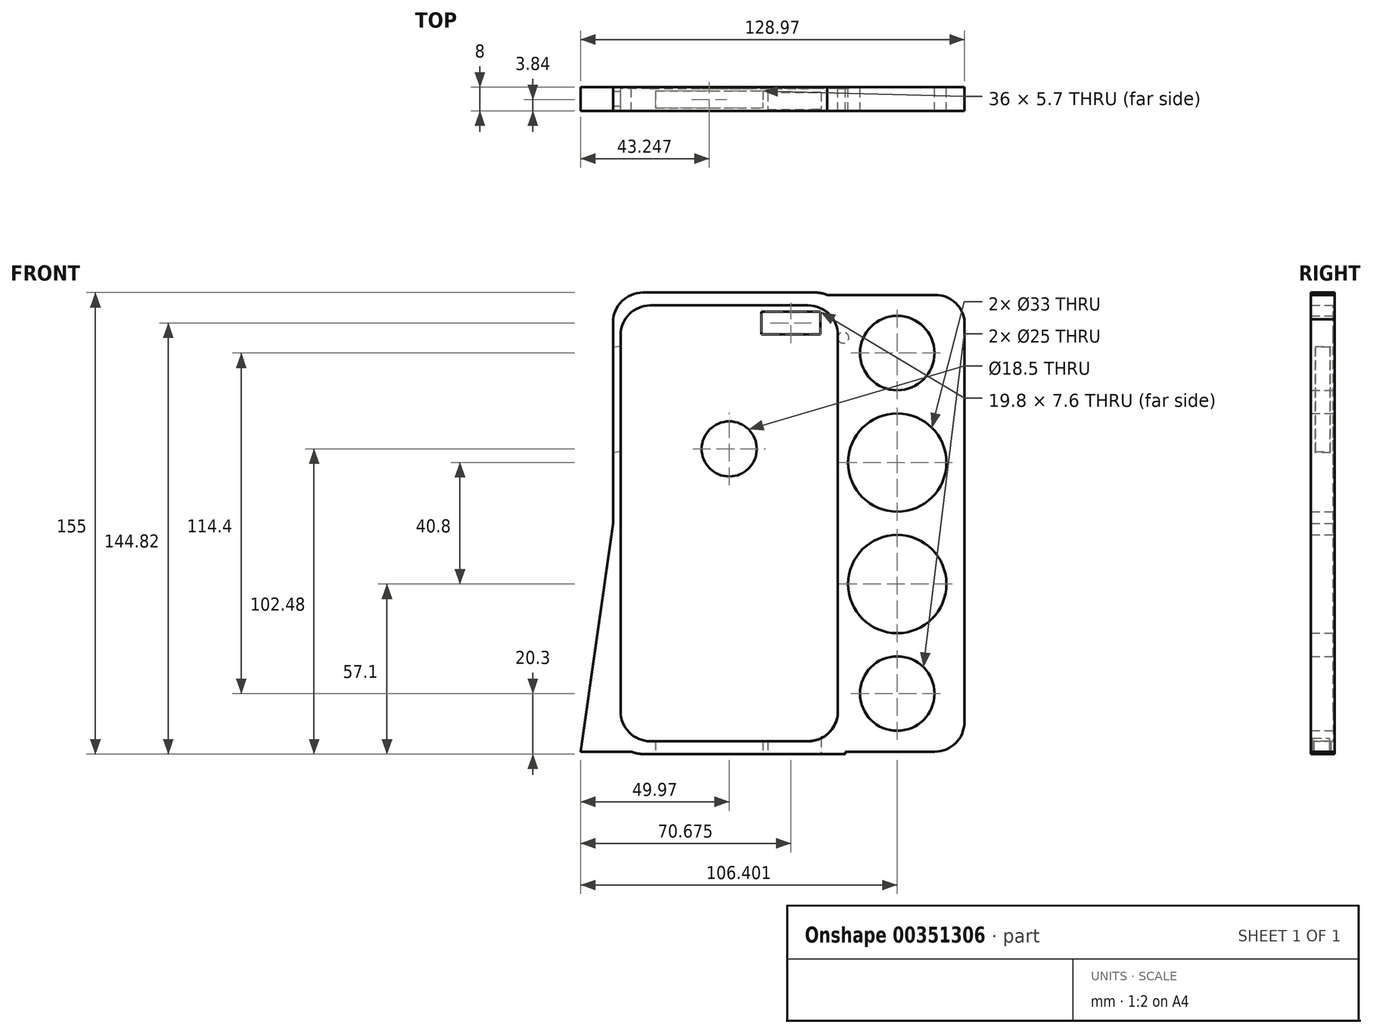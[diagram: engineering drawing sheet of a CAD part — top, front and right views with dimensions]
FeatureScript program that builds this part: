
annotation { "Feature Type Name" : "Feature", "Feature Type Description" : "" }
export const myFeature = defineFeature(function(context is Context, id is Id, definition is map)
    precondition{}
    {
        {
            var Q0;
            Q0=qCreatedBy(makeId("Front.planeOp"),FACE);
            var sketch = newSketch(context, id + "F0", { "sketchPlane" : qUnion([Q0])});
            skLineSegment(sketch, "E0.bottom", {"start": v(-29, -77.5) * mm, "end": v(39, -77.5) * mm});
            skLineSegment(sketch, "E0.top", {"start": v(-29, 77.5) * mm, "end": v(29, 77.5) * mm});
            skLineSegment(sketch, "E0.left", {"start": v(-39, -67.5) * mm, "end": v(-39, 67.5) * mm});
            skLineSegment(sketch, "E0.right", {"start": v(39, -77.5) * mm, "end": v(39, 77.5) * mm});
            skPoint(sketch, "E0.middle", {"position": v(0, 0) * mm});
            skLineSegment(sketch, "E1.bottom", {"start": v(39, 77.5) * mm, "end": v(79, 77.5) * mm});
            skLineSegment(sketch, "E1.top", {"start": v(39, -77.5) * mm, "end": v(79, -77.5) * mm});
            skLineSegment(sketch, "E1.left", {"start": v(39, 67.5) * mm, "end": v(39, -77.5) * mm});
            skLineSegment(sketch, "E1.right", {"start": v(79, 77.5) * mm, "end": v(79, -66.72) * mm});
            skCircle(sketch, "E2", {"center": v(56.43, 57.2) * mm, "radius": 12.5 * mm});
            skCircle(sketch, "E3", {"center": v(56.43, 20.4) * mm, "radius": 16.5 * mm});
            skCircle(sketch, "E4", {"center": v(56.43, -20.4) * mm, "radius": 16.5 * mm});
            skCircle(sketch, "E5", {"center": v(56.43, -57.2) * mm, "radius": 12.5 * mm});
            skPoint(sketch, "E6.visualSharp", {"position": v(-39, 77.5) * mm});
            skArc(sketch, "E6.filletArc", {"start": v(-29, 77.5) * mm, "mid": v(-36.07, 74.57) * mm, "end": v(-39, 67.5) * mm});
            skPoint(sketch, "E7.visualSharp", {"position": v(-39, -77.5) * mm});
            skArc(sketch, "E7.filletArc", {"start": v(-39, -67.5) * mm, "mid": v(-36.07, -74.57) * mm, "end": v(-29, -77.5) * mm});
            skPoint(sketch, "E8.visualSharp", {"position": v(39, 77.5) * mm});
            skArc(sketch, "E8.filletArc", {"start": v(39, 67.5) * mm, "mid": v(36.07, 74.57) * mm, "end": v(29, 77.5) * mm});
            skLineSegment(sketch, "E9.bottom", {"start": v(-49.97, -76.72) * mm, "end": v(69, -76.72) * mm});
            skLineSegment(sketch, "E9.top", {"start": v(-49.97, 76.72) * mm, "end": v(69.18, 76.72) * mm});
            skLineSegment(sketch, "E9.right", {"start": v(79.18, -76.72) * mm, "end": v(79.18, 66.72) * mm});
            skLineSegment(sketch, "E10", {"start": v(-49.97, 76.72) * mm, "end": v(-39, 0) * mm});
            skLineSegment(sketch, "E11", {"start": v(-39, 0) * mm, "end": v(-49.97, -76.72) * mm});
            skLineSegment(sketch, "E12.bottom", {"start": v(-26.5, -73.2) * mm, "end": v(26.5, -73.2) * mm});
            skLineSegment(sketch, "E12.top", {"start": v(-26.5, 73.2) * mm, "end": v(26.5, 73.2) * mm});
            skLineSegment(sketch, "E12.left", {"start": v(-36.5, -63.2) * mm, "end": v(-36.5, 63.2) * mm});
            skLineSegment(sketch, "E12.right", {"start": v(36.5, -63.2) * mm, "end": v(36.5, 63.2) * mm});
            skPoint(sketch, "E13.visualSharp", {"position": v(-36.5, 73.2) * mm});
            skArc(sketch, "E13.filletArc", {"start": v(-26.5, 73.2) * mm, "mid": v(-33.57, 70.26) * mm, "end": v(-36.5, 63.2) * mm});
            skPoint(sketch, "E14.visualSharp", {"position": v(36.5, 73.2) * mm});
            skArc(sketch, "E14.filletArc", {"start": v(36.5, 63.2) * mm, "mid": v(33.57, 70.26) * mm, "end": v(26.5, 73.2) * mm});
            skPoint(sketch, "E15.visualSharp", {"position": v(36.5, -73.2) * mm});
            skArc(sketch, "E15.filletArc", {"start": v(26.5, -73.2) * mm, "mid": v(33.57, -70.26) * mm, "end": v(36.5, -63.2) * mm});
            skPoint(sketch, "E16.visualSharp", {"position": v(-36.5, -73.2) * mm});
            skArc(sketch, "E16.filletArc", {"start": v(-36.5, -63.2) * mm, "mid": v(-33.57, -70.26) * mm, "end": v(-26.5, -73.2) * mm});
            skPoint(sketch, "E17.visualSharp", {"position": v(79.18, 76.72) * mm});
            skArc(sketch, "E17.filletArc", {"start": v(79.18, 66.72) * mm, "mid": v(76.25, 73.8) * mm, "end": v(69.18, 76.72) * mm});
            skPoint(sketch, "E18.newPointA", {"position": v(79.18, -76.72) * mm});
            skArc(sketch, "E18.filletArc", {"start": v(69, -76.72) * mm, "mid": v(76.07, -73.8) * mm, "end": v(79, -66.72) * mm});
            skPoint(sketch, "E9.left.end.orphan", {"position": v(-79.18, 76.72) * mm});
            skPoint(sketch, "E19.orphan", {"position": v(-79.18, -76.72) * mm});
            skSolve(sketch);
        }
        {
            var Q0;
            Q0=makeQuery(id+"F0.imprint","IMPRINT",FACE,{"disambiguationData":[TD([[makeQuery(id+"F0.imprint","IMPRINT",EDGE,{"derivedFrom":sQuery(id+"F0.wireOp",EDGE,"E12.bottom")}),1.0]])]});
            extrude(context, id + "F1", {"entities" : qUnion([Q0]), "depth" : .5 * mm});
        }
        {
            var Q0;
            {var subQ0=sQuery(id+"F0.wireOp",EDGE,"E0.bottom");Q0=makeQuery(id+"F0.imprint","IMPRINT",FACE,{"disambiguationData":[TD([[makeQuery(id+"F0.imprint","IMPRINT",EDGE,{"derivedFrom":subQ0}),1.0]])]});}
            var Q1;
            {var subQ0=sQuery(id+"F0.wireOp",EDGE,"E0.top");Q1=makeQuery(id+"F0.imprint","IMPRINT",FACE,{"disambiguationData":[TD([[makeQuery(id+"F0.imprint","IMPRINT",EDGE,{"derivedFrom":subQ0}),-1.0]])]});}
            var Q2;
            {var subQ3=sQuery(id+"F0.wireOp",EDGE,"E11");Q2=makeQuery(id+"F0.imprint","IMPRINT",FACE,{"disambiguationData":[TD([[makeQuery(id+"F0.imprint","IMPRINT",EDGE,{"derivedFrom":subQ3}),1.0]])]});}
            var Q3;
            {var subQ3=sQuery(id+"F0.wireOp",EDGE,"E10");Q3=makeQuery(id+"F0.imprint","IMPRINT",FACE,{"disambiguationData":[TD([[makeQuery(id+"F0.imprint","IMPRINT",EDGE,{"derivedFrom":subQ3}),1.0]])]});}
            var Q4;
            {var subQ1=sQuery(id+"F0.wireOp",EDGE,"E0.right");var subQ3=sQuery(id+"F0.wireOp",EDGE,"E9.top");var subQ4=makeQuery(id+"F0.imprint","INTERSECT",VERTEX,{"derivedFrom":[subQ1,subQ3]});Q4=makeQuery(id+"F0.imprint","IMPRINT",FACE,{"disambiguationData":[TD([[makeQuery(id+"F0.imprint","IMPRINT",EDGE,{"disambiguationData":[TD([[subQ4,1.0]])],"derivedFrom":subQ3}),-1.0]])]});}
            var Q5;
            Q5=makeQuery(id+"F0.imprint","IMPRINT",FACE,{"disambiguationData":[TD([[makeQuery(id+"F0.imprint","IMPRINT",EDGE,{"derivedFrom":sQuery(id+"F0.wireOp",EDGE,"E12.bottom")}),-1.0]])]});
            var Q6;
            Q6=makeQuery(id+"F0.imprint","IMPRINT",FACE,{"disambiguationData":[TD([[makeQuery(id+"F0.imprint","IMPRINT",EDGE,{"derivedFrom":sQuery(id+"F0.wireOp",EDGE,"E2")}),-1.0]])]});
            extrude(context, id + "F2", {"entities" : qUnion([Q0, Q1, Q2, Q3, Q4, Q5, Q6]), "depth" : 8 * mm});
        }
        {
            var Q0;
            Q0=makeQuery(id+"F2.opExtrude","SWEPT_FACE",FACE,{"disambiguationData":[OSD([sQuery(id+"F0.wireOp",EDGE,"E10")])]});
            var sketch = newSketch(context, id + "F3", { "sketchPlane" : qUnion([Q0])});
            skLineSegment(sketch, "E20.bottom", {"start": v(6.5, 64.02) * mm, "end": v(1.5, 64.02) * mm});
            skLineSegment(sketch, "E20.top", {"start": v(6.5, 29.02) * mm, "end": v(1.5, 29.02) * mm});
            skLineSegment(sketch, "E20.left", {"start": v(6.5, 64.02) * mm, "end": v(6.5, 29.02) * mm});
            skLineSegment(sketch, "E20.right", {"start": v(1.5, 64.02) * mm, "end": v(1.5, 29.02) * mm});
            skSolve(sketch);
        }
        {
            var Q0;
            Q0 = qSketchRegion(id + "F3", true);
            extrude(context, id + "F4", {"entities" : qUnion([Q0]), "operationType" : NewBodyOperationType.REMOVE, "oppositeDirection" : true, "depth" : 25 * mm});
        }
        {
            var Q0;
            Q0=makeQuery(id+"F1.opExtrude","CAP_FACE",FACE,{"disambiguationData":[OSD([sQuery(id+"F0.wireOp",EDGE,"E12.bottom"),sQuery(id+"F0.wireOp",EDGE,"E12.top"),sQuery(id+"F0.wireOp",EDGE,"E12.left"),sQuery(id+"F0.wireOp",EDGE,"E12.right"),sQuery(id+"F0.wireOp",EDGE,"E13.filletArc"),sQuery(id+"F0.wireOp",EDGE,"E14.filletArc"),sQuery(id+"F0.wireOp",EDGE,"E15.filletArc"),sQuery(id+"F0.wireOp",EDGE,"E16.filletArc")])],"isStart":false});
            var sketch = newSketch(context, id + "F5", { "sketchPlane" : qUnion([Q0])});
            skCircle(sketch, "E21", {"center": v(38.3, 62.35) * mm, "radius": 1.85 * mm});
            skCircle(sketch, "E22", {"center": v(0, 24.98) * mm, "radius": 9.25 * mm});
            skPoint(sketch, "E23.center.orphan", {"position": v(26.4, 62.35) * mm});
            skLineSegment(sketch, "E24.bottom", {"start": v(30.6, 71.12) * mm, "end": v(10.8, 71.12) * mm});
            skLineSegment(sketch, "E24.top", {"start": v(30.6, 63.52) * mm, "end": v(10.8, 63.52) * mm});
            skLineSegment(sketch, "E24.left", {"start": v(30.6, 71.12) * mm, "end": v(30.6, 63.52) * mm});
            skLineSegment(sketch, "E24.right", {"start": v(10.8, 71.12) * mm, "end": v(10.8, 63.52) * mm});
            skSolve(sketch);
        }
        {
            var Q0;
            Q0 = qSketchRegion(id + "F5", true);
            extrude(context, id + "F6", {"entities" : qUnion([Q0]), "operationType" : NewBodyOperationType.REMOVE, "oppositeDirection" : true, "depth" : 25 * mm});
        }
        {
            var Q0;
            Q0=makeQuery(id+"F2.opExtrude","SWEPT_FACE",FACE,{"disambiguationData":[OSD([sQuery(id+"F0.wireOp",EDGE,"E0.bottom")])]});
            var sketch = newSketch(context, id + "F7", { "sketchPlane" : qUnion([Q0])});
            skLineSegment(sketch, "E25.bottom", {"start": v(-24.72, 1.3) * mm, "end": v(11.28, 1.3) * mm});
            skLineSegment(sketch, "E25.top", {"start": v(-24.72, 7) * mm, "end": v(11.28, 7) * mm});
            skLineSegment(sketch, "E25.left", {"start": v(-24.72, 1.3) * mm, "end": v(-24.72, 7) * mm});
            skLineSegment(sketch, "E25.right", {"start": v(11.28, 1.3) * mm, "end": v(11.28, 7) * mm});
            skLineSegment(sketch, "E26.bottom", {"start": v(12.9, 1.76) * mm, "end": v(30.85, 1.76) * mm});
            skLineSegment(sketch, "E26.top", {"start": v(12.9, 7.46) * mm, "end": v(30.85, 7.46) * mm});
            skLineSegment(sketch, "E26.left", {"start": v(12.9, 1.76) * mm, "end": v(12.9, 7.46) * mm});
            skLineSegment(sketch, "E26.right", {"start": v(30.85, 1.76) * mm, "end": v(30.85, 7.46) * mm});
            skSolve(sketch);
        }
        {
            var Q0;
            Q0=makeQuery(id+"F7.imprint","IMPRINT",FACE,{"disambiguationData":[TD([[makeQuery(id+"F7.imprint","IMPRINT",EDGE,{"derivedFrom":sQuery(id+"F7.wireOp",EDGE,"E25.bottom")}),1.0]])]});
            var Q1;
            Q1=makeQuery(id+"F7.imprint","IMPRINT",FACE,{"disambiguationData":[TD([[makeQuery(id+"F7.imprint","IMPRINT",EDGE,{"derivedFrom":sQuery(id+"F7.wireOp",EDGE,"E26.bottom")}),1.0]])]});
            extrude(context, id + "F8", {"entities" : qUnion([Q0, Q1]), "operationType" : NewBodyOperationType.REMOVE, "endBound" : BoundingType.UP_TO_NEXT, "oppositeDirection" : true, "depth" : 25 * mm});
        }
        {
            var Q0;
            {var subQ3=sQuery(id+"F0.wireOp",EDGE,"E10");Q0=makeQuery(id+"F0.imprint","IMPRINT",FACE,{"disambiguationData":[TD([[makeQuery(id+"F0.imprint","IMPRINT",EDGE,{"derivedFrom":subQ3}),1.0]])]});}
            extrude(context, id + "F9", {"entities" : qUnion([Q0]), "operationType" : NewBodyOperationType.REMOVE, "depth" : 25 * mm});
        }
    });
